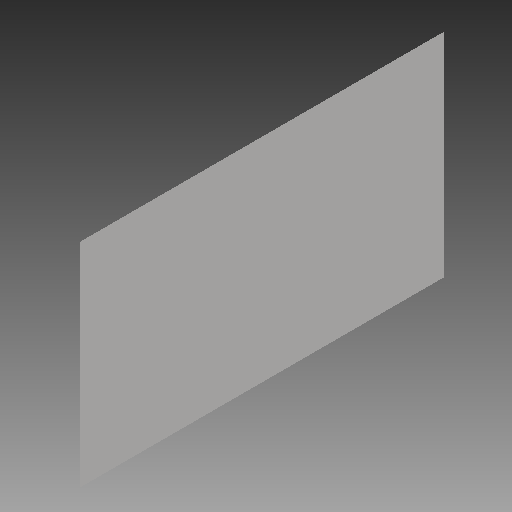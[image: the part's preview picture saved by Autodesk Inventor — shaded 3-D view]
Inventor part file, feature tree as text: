
AUTODESK INVENTOR PART (.ipt)
format: ipt  version: 2018.2 (Build 222227000, 227)  size: 84,992 bytes
history: native  units: mm
features: extrude x1, chamfer x1, sketch x1
ambient origin geometry x8: Origin, YZ Plane, XZ Plane, XY Plane, X Axis, Y Axis, Z Axis, Center Point
bodies: Volumenkörper1 (feature_tree)
feature tree (3):
  extrude  "Extrusion1"  Depth=20.0mm
  chamfer  "Fase1"  Distance=20.0mm
  sketch  "Skizze1"  dims[d0=350.0mm d1=600.0mm d2=20.0mm d3=0.0mm d4=20.0mm d5=2.0mm d6=45.0deg]
